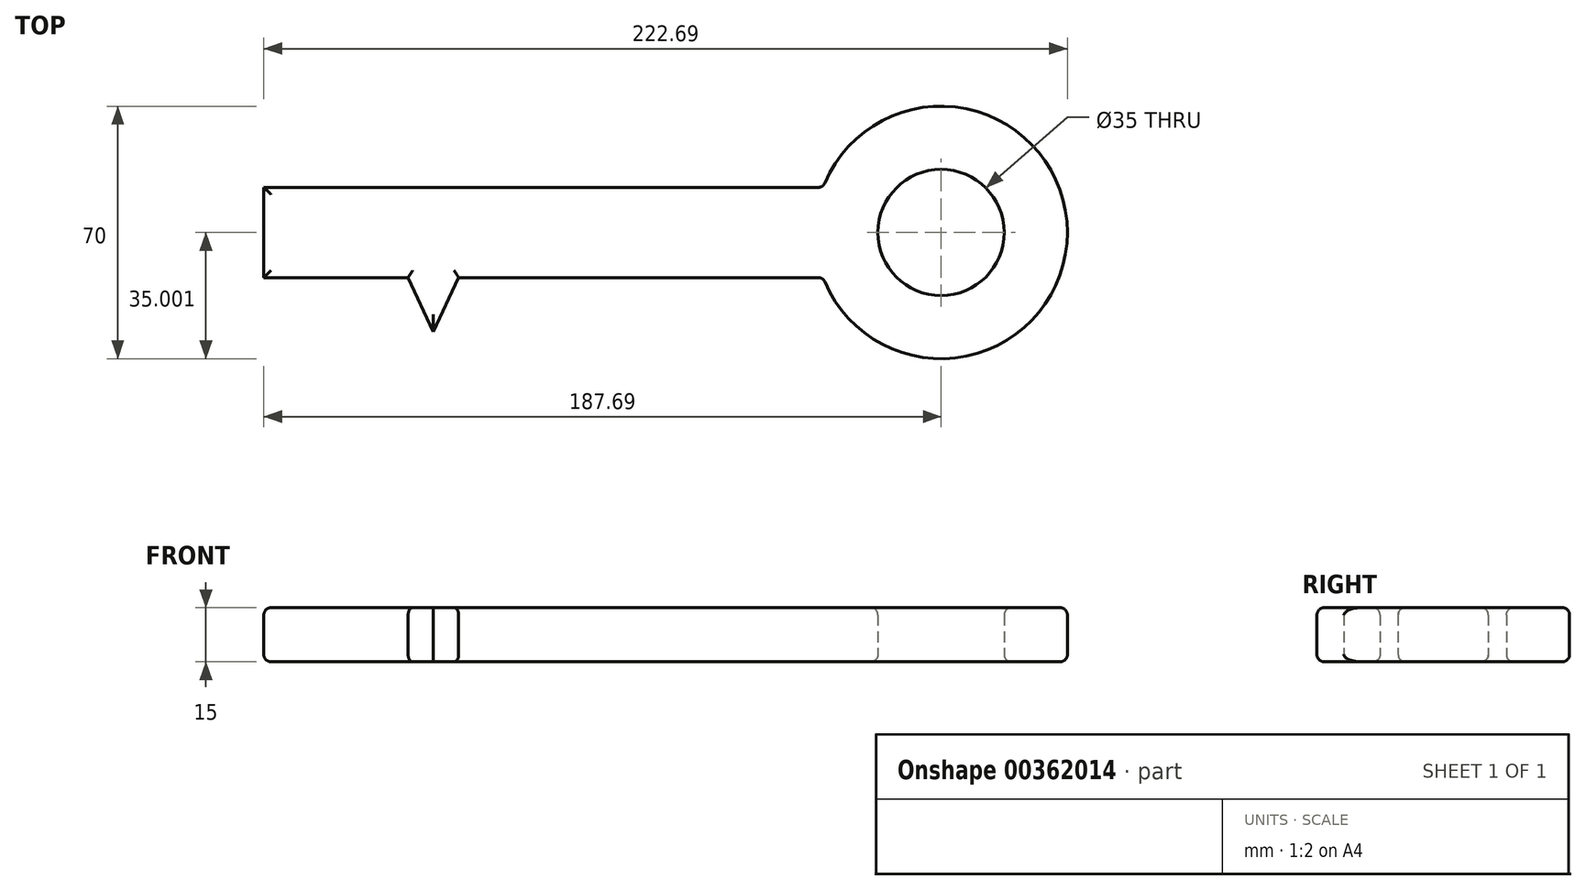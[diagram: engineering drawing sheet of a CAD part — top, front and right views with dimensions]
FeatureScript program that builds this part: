
annotation { "Feature Type Name" : "Feature", "Feature Type Description" : "" }
export const myFeature = defineFeature(function(context is Context, id is Id, definition is map)
    precondition{}
    {
        {
            var Q0;
            Q0=qCreatedBy(makeId("Top.planeOp"),FACE);
            var sketch = newSketch(context, id + "F0", { "sketchPlane" : qUnion([Q0])});
            skLineSegment(sketch, "E0.bottom", {"start": v(-77.83, 7.35) * mm, "end": v(77.17, 7.35) * mm});
            skLineSegment(sketch, "E0.top", {"start": v(-77.83, -17.65) * mm, "end": v(77.17, -17.65) * mm});
            skLineSegment(sketch, "E0.left", {"start": v(-77.83, 7.35) * mm, "end": v(-77.83, -17.65) * mm});
            skLineSegment(sketch, "E0.right", {"start": v(77.17, 7.35) * mm, "end": v(77.17, -17.65) * mm});
            skCircle(sketch, "E1", {"center": v(109.86, -5.15) * mm, "radius": 17.5 * mm});
            skLineSegment(sketch, "E2", {"start": v(-37.83, -17.65) * mm, "end": v(-30.83, -32.65) * mm});
            skLineSegment(sketch, "E3", {"start": v(-30.83, -32.65) * mm, "end": v(-23.83, -17.65) * mm});
            skLineSegment(sketch, "E4.bottom", {"start": v(-57.83, -17.65) * mm, "end": v(-47.83, -17.65) * mm});
            skLineSegment(sketch, "E4.top", {"start": v(-57.83, -32.65) * mm, "end": v(-47.83, -32.65) * mm});
            skLineSegment(sketch, "E4.left", {"start": v(-57.83, -17.65) * mm, "end": v(-57.83, -32.65) * mm});
            skLineSegment(sketch, "E4.right", {"start": v(-47.83, -17.65) * mm, "end": v(-47.83, -32.65) * mm});
            skArc(sketch, "E5", {"start": v(77.17, -17.65) * mm, "mid": v(144.86, -5.15) * mm, "end": v(77.17, 7.35) * mm});
            skLineSegment(sketch, "E6.bottom", {"start": v(-77.83, -17.65) * mm, "end": v(-67.83, -17.65) * mm});
            skLineSegment(sketch, "E6.top", {"start": v(-77.83, -47.65) * mm, "end": v(-67.83, -47.65) * mm});
            skLineSegment(sketch, "E6.left", {"start": v(-77.83, -17.65) * mm, "end": v(-77.83, -47.65) * mm});
            skLineSegment(sketch, "E6.right", {"start": v(-67.83, -17.65) * mm, "end": v(-67.83, -47.65) * mm});
            skSolve(sketch);
        }
        {
            var Q0;
            Q0=makeQuery(id+"F0.imprint","IMPRINT",FACE,{"disambiguationData":[TD([[makeQuery(id+"F0.imprint","IMPRINT",EDGE,{"derivedFrom":sQuery(id+"F0.wireOp",EDGE,"E0.bottom")}),-1.0]])]});
            var Q1;
            Q1=makeQuery(id+"F0.imprint","IMPRINT",FACE,{"disambiguationData":[TD([[makeQuery(id+"F0.imprint","IMPRINT",EDGE,{"derivedFrom":sQuery(id+"F0.wireOp",EDGE,"E4.bottom")}),-1.0]])]});
            var Q2;
            {var subQ0=sQuery(id+"F0.wireOp",EDGE,"E2");Q2=makeQuery(id+"F0.imprint","IMPRINT",FACE,{"disambiguationData":[TD([[makeQuery(id+"F0.imprint","IMPRINT",EDGE,{"derivedFrom":subQ0}),1.0]])]});}
            var Q3;
            Q3=makeQuery(id+"F0.imprint","IMPRINT",FACE,{"disambiguationData":[TD([[makeQuery(id+"F0.imprint","IMPRINT",EDGE,{"derivedFrom":sQuery(id+"F0.wireOp",EDGE,"E0.right")}),1.0]])]});
            var Q4;
            Q4=makeQuery(id+"F0.imprint","IMPRINT",FACE,{"disambiguationData":[TD([[makeQuery(id+"F0.imprint","IMPRINT",EDGE,{"derivedFrom":sQuery(id+"F0.wireOp",EDGE,"E6.bottom")}),-1.0]])]});
            extrude(context, id + "F1", {"entities" : qUnion([Q0, Q1, Q2, Q3, Q4]), "depth" : 15 * mm});
        }
        {
            var Q0;
            Q0=makeQuery(id+"F1.opExtrude","CAP_EDGE",EDGE,{"disambiguationData":[OSD([sQuery(id+"F0.wireOp",EDGE,"E0.bottom")])],"isStart":true});
            var Q1;
            {var subQ0=sQuery(id+"F0.wireOp",EDGE,"E0.top");Q1=makeQuery(id+"F1.opExtrude","CAP_EDGE",EDGE,{"disambiguationData":[OSD([subQ0]),TDD([makeQuery(id+"F0.imprint","IMPRINT",EDGE,{"disambiguationData":[TD([[makeQuery(id+"F0.imprint","INTERSECT",VERTEX,{"derivedFrom":[subQ0,sQuery(id+"F0.wireOp",EDGE,"E3")]}),-1.0]])],"derivedFrom":subQ0})])],"isStart":true});}
            var Q2;
            Q2=makeQuery(id+"F1.opExtrude","CAP_EDGE",EDGE,{"disambiguationData":[OSD([sQuery(id+"F0.wireOp",EDGE,"E3")])],"isStart":true});
            var Q3;
            Q3=makeQuery(id+"F1.opExtrude","CAP_EDGE",EDGE,{"disambiguationData":[OSD([sQuery(id+"F0.wireOp",EDGE,"E2")])],"isStart":true});
            var Q4;
            {var subQ0=sQuery(id+"F0.wireOp",EDGE,"E0.top");Q4=makeQuery(id+"F1.opExtrude","CAP_EDGE",EDGE,{"disambiguationData":[OSD([subQ0]),TDD([makeQuery(id+"F0.imprint","IMPRINT",EDGE,{"disambiguationData":[TD([[makeQuery(id+"F0.imprint","INTERSECT",VERTEX,{"derivedFrom":[subQ0,sQuery(id+"F0.wireOp",EDGE,"E2")]}),1.0]])],"derivedFrom":subQ0})])],"isStart":true});}
            var Q5;
            Q5=makeQuery(id+"F1.opExtrude","CAP_EDGE",EDGE,{"disambiguationData":[OSD([sQuery(id+"F0.wireOp",EDGE,"E4.right")])],"isStart":true});
            var Q6;
            Q6=makeQuery(id+"F1.opExtrude","CAP_EDGE",EDGE,{"disambiguationData":[OSD([sQuery(id+"F0.wireOp",EDGE,"E4.top")])],"isStart":true});
            var Q7;
            Q7=makeQuery(id+"F1.opExtrude","CAP_EDGE",EDGE,{"disambiguationData":[OSD([sQuery(id+"F0.wireOp",EDGE,"E0.left"),sQuery(id+"F0.wireOp",EDGE,"E6.left")])],"isStart":true});
            var Q8;
            {var subQ0=sQuery(id+"F0.wireOp",EDGE,"E0.top");Q8=makeQuery(id+"F1.opExtrude","CAP_EDGE",EDGE,{"disambiguationData":[OSD([subQ0]),TDD([makeQuery(id+"F0.imprint","IMPRINT",EDGE,{"disambiguationData":[TD([[makeQuery(id+"F0.imprint","INTERSECT",VERTEX,{"derivedFrom":[subQ0,sQuery(id+"F0.wireOp",EDGE,"E6.bottom"),sQuery(id+"F0.wireOp",EDGE,"E6.right")]}),-1.0]])],"derivedFrom":subQ0})])],"isStart":true});}
            var Q9;
            Q9=makeQuery(id+"F1.opExtrude","CAP_EDGE",EDGE,{"disambiguationData":[OSD([sQuery(id+"F0.wireOp",EDGE,"E4.left")])],"isStart":true});
            var Q10;
            Q10=makeQuery(id+"F1.opExtrude","CAP_EDGE",EDGE,{"disambiguationData":[OSD([sQuery(id+"F0.wireOp",EDGE,"E6.top")])],"isStart":true});
            var Q11;
            Q11=makeQuery(id+"F1.opExtrude","CAP_EDGE",EDGE,{"disambiguationData":[OSD([sQuery(id+"F0.wireOp",EDGE,"E6.right")])],"isStart":true});
            var Q12;
            Q12=makeQuery(id+"F1.opExtrude","SWEPT_FACE",FACE,{"disambiguationData":[OSD([sQuery(id+"F0.wireOp",EDGE,"E5")])]});
            var Q13;
            Q13=makeQuery(id+"F1.opExtrude","CAP_EDGE",EDGE,{"disambiguationData":[OSD([sQuery(id+"F0.wireOp",EDGE,"E1")])],"isStart":true});
            var Q14;
            Q14=makeQuery(id+"F1.opExtrude","CAP_FACE",FACE,{"disambiguationData":[OSD([sQuery(id+"F0.wireOp",EDGE,"E0.bottom"),sQuery(id+"F0.wireOp",EDGE,"E0.top"),sQuery(id+"F0.wireOp",EDGE,"E0.left"),sQuery(id+"F0.wireOp",EDGE,"E1"),sQuery(id+"F0.wireOp",EDGE,"E2"),sQuery(id+"F0.wireOp",EDGE,"E3"),sQuery(id+"F0.wireOp",EDGE,"E4.top"),sQuery(id+"F0.wireOp",EDGE,"E4.left"),sQuery(id+"F0.wireOp",EDGE,"E4.right"),sQuery(id+"F0.wireOp",EDGE,"E5"),sQuery(id+"F0.wireOp",EDGE,"E6.top"),sQuery(id+"F0.wireOp",EDGE,"E6.left"),sQuery(id+"F0.wireOp",EDGE,"E6.right")])],"isStart":false});
            fillet(context, id + "F2", {"entities" : qUnion([Q0, Q1, Q2, Q3, Q4, Q5, Q6, Q7, Q8, Q9, Q10, Q11, Q12, Q13, Q14]), "radius" : 2 * mm, "tangentPropagation" : true, "allowEdgeOverflow" : false});
        }
    });
